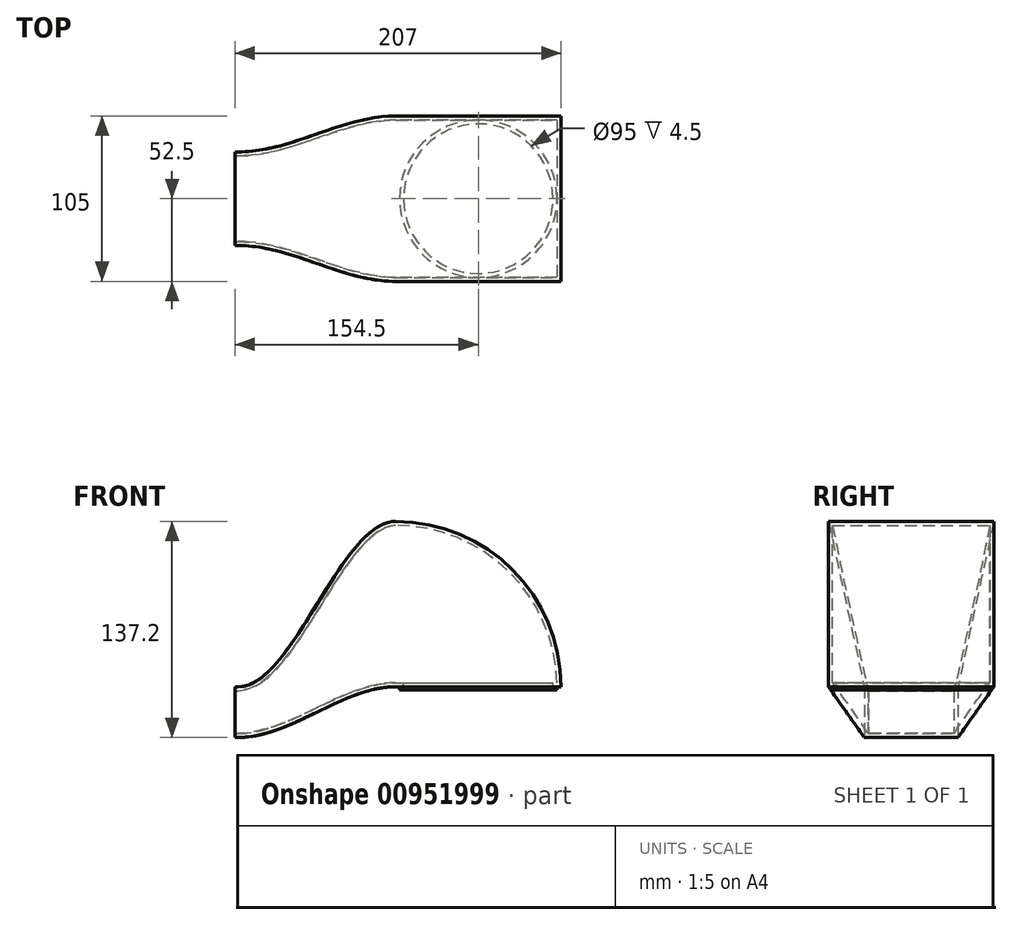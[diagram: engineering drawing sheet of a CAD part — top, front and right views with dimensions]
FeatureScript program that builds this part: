
annotation { "Feature Type Name" : "Feature", "Feature Type Description" : "" }
export const myFeature = defineFeature(function(context is Context, id is Id, definition is map)
    precondition{}
    {
        {
            var Q0;
            Q0=qCreatedBy(makeId("Right.planeOp"),FACE);
            var sketch = newSketch(context, id + "F0", { "sketchPlane" : qUnion([Q0])});
            skLineSegment(sketch, "E0.bottom", {"start": v(-29.75, 32.2) * mm, "end": v(29.75, 32.2) * mm});
            skLineSegment(sketch, "E0.top", {"start": v(-29.75, 0) * mm, "end": v(29.75, 0) * mm});
            skLineSegment(sketch, "E0.left", {"start": v(-29.75, 32.2) * mm, "end": v(-29.75, 0) * mm});
            skLineSegment(sketch, "E0.right", {"start": v(29.75, 32.2) * mm, "end": v(29.75, 0) * mm});
            skSolve(sketch);
        }
        {
            var Q0;
            Q0=qCreatedBy(makeId("Right.planeOp"),FACE);
            cPlane(context, id + "F1", {"entities" : qUnion([Q0]), "cplaneType" : CPlaneType.OFFSET, "offset" : 100 * mm, "width" : 150 * mm, "height" : 150 * mm});
        }
        {
            var Q0;
            Q0=qCreatedBy(id+"F1.planeOp",FACE);
            var sketch = newSketch(context, id + "F2", { "sketchPlane" : qUnion([Q0])});
            skLineSegment(sketch, "E1.bottom", {"start": v(-52.5, 32.2) * mm, "end": v(52.5, 32.2) * mm});
            skLineSegment(sketch, "E1.top", {"start": v(-52.5, 137.2) * mm, "end": v(52.5, 137.2) * mm});
            skLineSegment(sketch, "E1.left", {"start": v(-52.5, 32.2) * mm, "end": v(-52.5, 137.2) * mm});
            skLineSegment(sketch, "E1.right", {"start": v(52.5, 32.2) * mm, "end": v(52.5, 137.2) * mm});
            skLineSegment(sketch, "E2", {"start": v(0, 0) * mm, "end": v(0, 32.2) * mm, "construction": true});
            skSolve(sketch);
        }
        {
            var Q0;
            Q0 = qSketchRegion(id + "F2", true);
            var Q1;
            Q1=sQuery(id+"F2.wireOp",EDGE,"E1.bottom");
            revolve(context, id + "F3", {"surfaceOperationType" : NewSurfaceOperationType.NEW, "entities" : qUnion([Q0]), "axis" : qUnion([Q1]), "revolveType" : RevolveType.ONE_DIRECTION, "angle" : 90 * degree});
        }
        {
            var Q0;
            Q0 = qSketchRegion(id + "F0", true);
            extrude(context, id + "F4", {"entities" : qUnion([Q0]), "oppositeDirection" : true, "depth" : 2 * mm, "offsetDistance" : 25 * mm});
        }
        {
            var Q0;
            Q0=makeQuery(id+"F3.opRevolve","CAP_FACE",FACE,{"disambiguationData":[OSD([sQuery(id+"F2.wireOp",EDGE,"E1.bottom"),sQuery(id+"F2.wireOp",EDGE,"E1.top"),sQuery(id+"F2.wireOp",EDGE,"E1.left"),sQuery(id+"F2.wireOp",EDGE,"E1.right")])],"isStart":false});
            var sketch = newSketch(context, id + "F5", { "sketchPlane" : qUnion([Q0])});
            skLineSegment(sketch, "E3", {"start": v(100, 52.5) * mm, "end": v(205, -52.5) * mm, "construction": true});
            skCircle(sketch, "E4", {"center": v(152.5, 0) * mm, "radius": 50 * mm});
            skSolve(sketch);
        }
        {
            var Q0;
            Q0 = qSketchRegion(id + "F5", true);
            extrude(context, id + "F6", {"entities" : qUnion([Q0]), "operationType" : NewBodyOperationType.ADD, "depth" : 2 * mm, "offsetDistance" : 25 * mm});
        }
        {
            var Q0;
            Q0=makeQuery(id+"F3.opRevolve","CAP_FACE",FACE,{"disambiguationData":[OSD([sQuery(id+"F2.wireOp",EDGE,"E1.bottom"),sQuery(id+"F2.wireOp",EDGE,"E1.top"),sQuery(id+"F2.wireOp",EDGE,"E1.left"),sQuery(id+"F2.wireOp",EDGE,"E1.right")])],"isStart":true});
            var Q1;
            Q1=makeQuery(id+"F4.opExtrude","CAP_FACE",FACE,{"disambiguationData":[OSD([sQuery(id+"F0.wireOp",EDGE,"E0.bottom"),sQuery(id+"F0.wireOp",EDGE,"E0.top"),sQuery(id+"F0.wireOp",EDGE,"E0.left"),sQuery(id+"F0.wireOp",EDGE,"E0.right")])],"isStart":true});
            loft(context, id + "F7", {"operationType" : NewBodyOperationType.ADD, "startCondition" : LoftEndDerivativeType.NORMAL_TO_PROFILE, "startMagnitude" : 1, "endCondition" : LoftEndDerivativeType.NORMAL_TO_PROFILE, "endMagnitude" : 1, "sheetProfilesArray" : [{ "sheetProfileEntities" : qUnion([Q0]) }, { "sheetProfileEntities" : qUnion([Q1]) }]});
        }
        {
            var Q0;
            Q0=makeQuery(id+"F6.opExtrude","CAP_FACE",FACE,{"disambiguationData":[OSD([sQuery(id+"F5.wireOp",EDGE,"E4")])],"isStart":false});
            var Q1;
            Q1=makeQuery(id+"F4.opExtrude","CAP_FACE",FACE,{"disambiguationData":[OSD([sQuery(id+"F0.wireOp",EDGE,"E0.bottom"),sQuery(id+"F0.wireOp",EDGE,"E0.top"),sQuery(id+"F0.wireOp",EDGE,"E0.left"),sQuery(id+"F0.wireOp",EDGE,"E0.right")])],"isStart":false});
            shell(context, id + "F8", {"entities" : qUnion([Q0, Q1]), "thickness" : 2.5 * mm});
        }
    });
